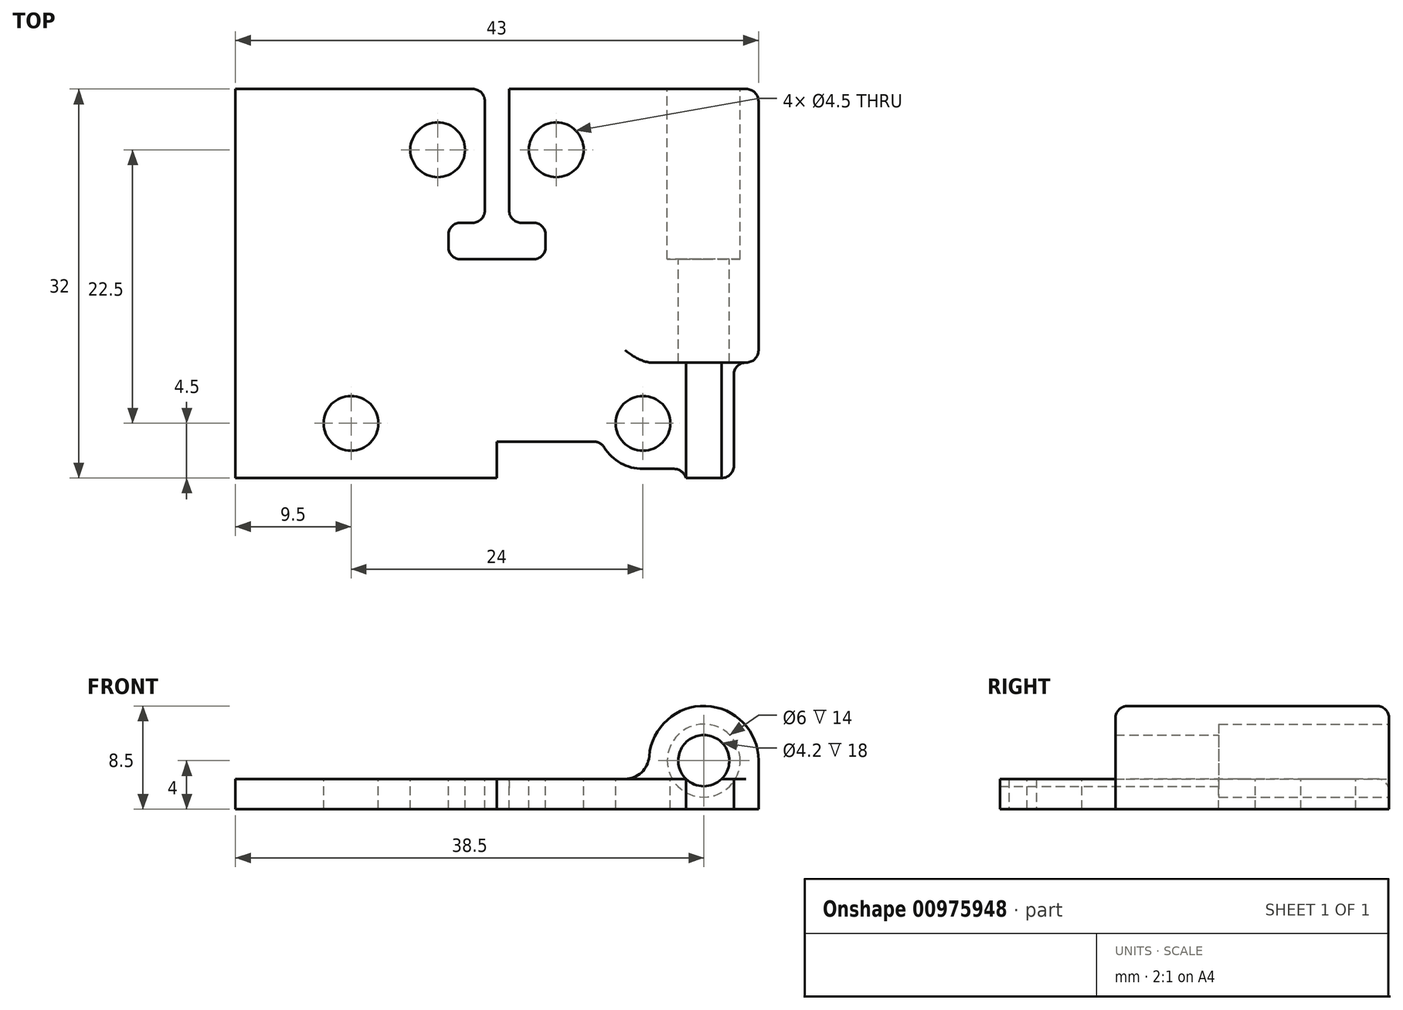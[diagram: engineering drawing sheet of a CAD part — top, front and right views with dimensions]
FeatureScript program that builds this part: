
annotation { "Feature Type Name" : "Feature", "Feature Type Description" : "" }
export const myFeature = defineFeature(function(context is Context, id is Id, definition is map)
    precondition{}
    {
        {
            var Q0;
            Q0=qCreatedBy(makeId("Top.planeOp"),FACE);
            var sketch = newSketch(context, id + "F0", { "sketchPlane" : qUnion([Q0])});
            skLineSegment(sketch, "E0.bottom", {"start": v(21.5, -16) * mm, "end": v(-21.5, -16) * mm});
            skLineSegment(sketch, "E0.top", {"start": v(21.5, 16) * mm, "end": v(-21.5, 16) * mm});
            skLineSegment(sketch, "E0.left", {"start": v(21.5, -16) * mm, "end": v(21.5, 16) * mm});
            skLineSegment(sketch, "E0.right", {"start": v(-21.5, -16) * mm, "end": v(-21.5, 16) * mm});
            skPoint(sketch, "E0.middle", {"position": v(0, 0) * mm});
            skSolve(sketch);
        }
        {
            var Q0;
            Q0 = qSketchRegion(id + "F0", true);
            extrude(context, id + "F1", {"entities" : qUnion([Q0]), "depth" : 2.5 * mm, "offsetDistance" : 25 * mm});
        }
        {
            var Q0;
            Q0=makeQuery(id+"F1.opExtrude","SWEPT_FACE",FACE,{"disambiguationData":[OSD([sQuery(id+"F0.wireOp",EDGE,"E0.top")])]});
            var sketch = newSketch(context, id + "F2", { "sketchPlane" : qUnion([Q0])});
            skLineSegment(sketch, "E1", {"start": v(0, 0) * mm, "end": v(0, 2.5) * mm, "construction": true});
            skLineSegment(sketch, "E2", {"start": v(-21.5, 4) * mm, "end": v(-21.5, 0) * mm});
            skLineSegment(sketch, "E3", {"start": v(-21.5, 0) * mm, "end": v(-12.5, 0) * mm});
            skLineSegment(sketch, "E4", {"start": v(-12.5, 0) * mm, "end": v(-12.5, 4) * mm});
            skArc(sketch, "E5.trimOffspring", {"start": v(-12.5, 4) * mm, "mid": v(-17, 8.5) * mm, "end": v(-21.5, 4) * mm});
            skSolve(sketch);
        }
        {
            var Q0;
            Q0 = qSketchRegion(id + "F2", true);
            extrude(context, id + "F3", {"entities" : qUnion([Q0]), "operationType" : NewBodyOperationType.ADD, "oppositeDirection" : true, "depth" : 22.5 * mm, "offsetDistance" : 25 * mm});
        }
        {
            var Q0;
            Q0=makeQuery(id+"F3.boolean.opBoolean","INTERSECT",EDGE,{"derivedFrom":[makeQuery(id+"F1.opExtrude","CAP_FACE",FACE,{"disambiguationData":[OSD([sQuery(id+"F0.wireOp",EDGE,"E0.bottom"),sQuery(id+"F0.wireOp",EDGE,"E0.top"),sQuery(id+"F0.wireOp",EDGE,"E0.left"),sQuery(id+"F0.wireOp",EDGE,"E0.right")])],"isStart":false}),makeQuery(id+"F3.opExtrude","SWEPT_FACE",FACE,{"disambiguationData":[OSD([sQuery(id+"F2.wireOp",EDGE,"E4")])]})]});
            fillet(context, id + "F4", {"entities" : qUnion([Q0]), "radius" : 2 * mm, "tangentPropagation" : true, "allowEdgeOverflow" : false});
        }
        {
            var Q0;
            Q0=makeQuery(id+"F3.boolean.opBoolean","MERGE",FACE,{"derivedFrom":[makeQuery(id+"F1.opExtrude","SWEPT_FACE",FACE,{"disambiguationData":[OSD([sQuery(id+"F0.wireOp",EDGE,"E0.top")])]}),makeQuery(id+"F3.opExtrude","CAP_FACE",FACE,{"disambiguationData":[OSD([sQuery(id+"F2.wireOp",EDGE,"E2"),sQuery(id+"F2.wireOp",EDGE,"E3"),sQuery(id+"F2.wireOp",EDGE,"E4"),sQuery(id+"F2.wireOp",EDGE,"E5.trimOffspring")])],"isStart":true})]});
            var sketch = newSketch(context, id + "F5", { "sketchPlane" : qUnion([Q0])});
            skArc(sketch, "E6.0", {"start": v(-12.51, 4.35) * mm, "mid": v(-17.17, 8.5) * mm, "end": v(-21.5, 4) * mm, "construction": true});
            skCircle(sketch, "E7", {"center": v(-17, 4) * mm, "radius": 3 * mm});
            skSolve(sketch);
        }
        {
            var Q0;
            Q0 = qSketchRegion(id + "F5", true);
            extrude(context, id + "F6", {"entities" : qUnion([Q0]), "operationType" : NewBodyOperationType.REMOVE, "oppositeDirection" : true, "depth" : 14 * mm, "offsetDistance" : 25 * mm});
        }
        {
            var Q0;
            Q0=makeQuery(id+"F6.boolean.opBoolean","COPY",FACE,{"derivedFrom":makeQuery(id+"F6.opExtrude","CAP_FACE",FACE,{"disambiguationData":[OSD([sQuery(id+"F5.wireOp",EDGE,"E7")])],"isStart":false})});
            var sketch = newSketch(context, id + "F7", { "sketchPlane" : qUnion([Q0])});
            skCircle(sketch, "E8", {"center": v(-17, 4) * mm, "radius": 2.1 * mm});
            skSolve(sketch);
        }
        {
            var Q0;
            Q0 = qSketchRegion(id + "F7", true);
            extrude(context, id + "F8", {"entities" : qUnion([Q0]), "operationType" : NewBodyOperationType.REMOVE, "oppositeDirection" : true, "depth" : 25 * mm, "offsetDistance" : 25 * mm});
        }
        {
            var Q0;
            Q0=makeQuery(id+"F1.opExtrude","CAP_FACE",FACE,{"disambiguationData":[OSD([sQuery(id+"F0.wireOp",EDGE,"E0.bottom"),sQuery(id+"F0.wireOp",EDGE,"E0.top"),sQuery(id+"F0.wireOp",EDGE,"E0.left"),sQuery(id+"F0.wireOp",EDGE,"E0.right")])],"isStart":false});
            var sketch = newSketch(context, id + "F9", { "sketchPlane" : qUnion([Q0])});
            skLineSegment(sketch, "E9", {"start": v(0, 16) * mm, "end": v(0, 0) * mm, "construction": true});
            skPoint(sketch, "E10", {"position": v(12, -11.5) * mm});
            skPoint(sketch, "E11", {"position": v(4.88, 11) * mm});
            skPoint(sketch, "E12.MirrorP", {"position": v(-4.88, 11) * mm});
            skPoint(sketch, "E13.MirrorP", {"position": v(-12, -11.5) * mm});
            skSolve(sketch);
        }
        {
            var Q0;
            Q0=sQuery(id+"F9.wireOp",VERTEX,"E11");
            var Q1;
            Q1=sQuery(id+"F9.wireOp",VERTEX,"E12.MirrorP");
            var Q2;
            Q2=sQuery(id+"F9.wireOp",VERTEX,"E13.MirrorP");
            var Q3;
            Q3=sQuery(id+"F9.wireOp",VERTEX,"E10");
            var Q4;
            Q4=makeQuery(id+"F1.opExtrude","SWEPT_BODY",BODY,{"disambiguationData":[OSD([sQuery(id+"F0.wireOp",EDGE,"E0.bottom"),sQuery(id+"F0.wireOp",EDGE,"E0.top"),sQuery(id+"F0.wireOp",EDGE,"E0.left"),sQuery(id+"F0.wireOp",EDGE,"E0.right")])]});
            hole(context, id + "F10", {"style" : HoleStyle.SIMPLE, "endStyle" : HoleEndStyle.THROUGH, "holeDiameter" : 4.5 * mm, "majorDiameter" : 5 * mm, "isTappedThrough" : true, "tappedDepth" : 12 * mm, "tapClearance" : 3, "locations" : qUnion([Q0, Q1, Q2, Q3]), "scope" : qUnion([Q4])});
        }
        {
            var Q0;
            Q0=makeQuery(id+"F1.opExtrude","CAP_FACE",FACE,{"disambiguationData":[OSD([sQuery(id+"F0.wireOp",EDGE,"E0.bottom"),sQuery(id+"F0.wireOp",EDGE,"E0.top"),sQuery(id+"F0.wireOp",EDGE,"E0.left"),sQuery(id+"F0.wireOp",EDGE,"E0.right")])],"isStart":false});
            var sketch = newSketch(context, id + "F11", { "sketchPlane" : qUnion([Q0])});
            skLineSegment(sketch, "E14", {"start": v(0, 16) * mm, "end": v(0, 0) * mm, "construction": true});
            skLineSegment(sketch, "E15", {"start": v(0, 16) * mm, "end": v(1, 16) * mm});
            skLineSegment(sketch, "E16", {"start": v(1, 16) * mm, "end": v(1, 5) * mm});
            skLineSegment(sketch, "E17", {"start": v(1, 5) * mm, "end": v(4, 5) * mm});
            skLineSegment(sketch, "E18", {"start": v(4, 5) * mm, "end": v(4, 2) * mm});
            skLineSegment(sketch, "E19", {"start": v(4, 2) * mm, "end": v(0, 2) * mm});
            skLineSegment(sketch, "E20.MirrorCS", {"start": v(0, 16) * mm, "end": v(-1, 16) * mm});
            skLineSegment(sketch, "E21.MirrorCS", {"start": v(-1, 16) * mm, "end": v(-1, 5) * mm});
            skLineSegment(sketch, "E22.MirrorCS", {"start": v(-1, 5) * mm, "end": v(-4, 5) * mm});
            skLineSegment(sketch, "E23.MirrorCS", {"start": v(-4, 5) * mm, "end": v(-4, 2) * mm});
            skLineSegment(sketch, "E24.MirrorCS", {"start": v(-4, 2) * mm, "end": v(0, 2) * mm});
            skSolve(sketch);
        }
        {
            var Q0;
            Q0 = qSketchRegion(id + "F11", true);
            extrude(context, id + "F12", {"entities" : qUnion([Q0]), "operationType" : NewBodyOperationType.REMOVE, "endBound" : BoundingType.UP_TO_NEXT, "oppositeDirection" : true, "depth" : 25 * mm, "offsetDistance" : 25 * mm});
        }
        {
            var Q0;
            {var subQ5=sQuery(id+"F0.wireOp",EDGE,"E0.top");var subQ6=makeQuery(id+"F1.opExtrude","SWEPT_FACE",FACE,{"disambiguationData":[OSD([subQ5])]});var subQ8=sQuery(id+"F0.wireOp",EDGE,"E0.bottom");var subQ10=sQuery(id+"F0.wireOp",EDGE,"E0.right");var subQ11=sQuery(id+"F0.wireOp",EDGE,"E0.left");Q0=makeQuery(id+"FoQRUGXMusNffjF_1.1.F8.boolean.opBoolean","SPLIT",FACE,{"disambiguationData":[TD([subQ6])],"derivedFrom":makeQuery(id+"F8.boolean.opBoolean","SPLIT",FACE,{"disambiguationData":[TD([subQ6])],"derivedFrom":makeQuery(id+"F1.opExtrude","CAP_FACE",FACE,{"disambiguationData":[OSD([subQ8,subQ5,subQ11,subQ10])],"isStart":false})})});}
            var sketch = newSketch(context, id + "F13", { "sketchPlane" : qUnion([Q0])});
            skLineSegment(sketch, "E25", {"start": v(0, 0) * mm, "end": v(0, -16) * mm, "construction": true});
            skLineSegment(sketch, "E26.bottom", {"start": v(21.5, -16) * mm, "end": v(19.47, -16) * mm});
            skLineSegment(sketch, "E26.top", {"start": v(21.5, -6.5) * mm, "end": v(19.47, -6.5) * mm});
            skLineSegment(sketch, "E26.left", {"start": v(21.5, -16) * mm, "end": v(21.5, -6.5) * mm});
            skLineSegment(sketch, "E26.right", {"start": v(19.47, -16) * mm, "end": v(19.47, -6.5) * mm});
            skArc(sketch, "E27.0", {"start": v(8.56, -13) * mm, "mid": v(9.95, -14.64) * mm, "end": v(12, -15.25) * mm});
            skLineSegment(sketch, "E28", {"start": v(12, -15.25) * mm, "end": v(15.53, -15.25) * mm});
            skLineSegment(sketch, "E29", {"start": v(0, -13) * mm, "end": v(8.56, -13) * mm});
            skLineSegment(sketch, "E30", {"start": v(0, -13) * mm, "end": v(0, -16) * mm});
            skLineSegment(sketch, "E31", {"start": v(0, -16) * mm, "end": v(15.53, -16) * mm});
            skLineSegment(sketch, "E32", {"start": v(15.53, -16) * mm, "end": v(15.53, -15.25) * mm});
            skSolve(sketch);
        }
        {
            var Q0;
            Q0 = qSketchRegion(id + "F13", true);
            extrude(context, id + "F14", {"entities" : qUnion([Q0]), "operationType" : NewBodyOperationType.REMOVE, "endBound" : BoundingType.UP_TO_NEXT, "oppositeDirection" : true, "depth" : 25 * mm, "offsetDistance" : 25 * mm});
        }
        {
            var Q0;
            Q0=makeQuery(id+"F14.boolean.opBoolean","COPY",EDGE,{"derivedFrom":makeQuery(id+"F14.opExtrude","SWEPT_EDGE",EDGE,{"disambiguationData":[OSD([sQuery(id+"F13.wireOp",EDGE,"E26.top"),sQuery(id+"F13.wireOp",EDGE,"E26.right")])]})});
            var Q1;
            Q1=makeQuery(id+"F14.boolean.opBoolean","COPY",EDGE,{"derivedFrom":makeQuery(id+"F14.opExtrude","SWEPT_EDGE",EDGE,{"disambiguationData":[OSD([sQuery(id+"F13.wireOp",EDGE,"E26.bottom"),sQuery(id+"F13.wireOp",EDGE,"E26.right")])]})});
            var Q2;
            Q2=makeQuery(id+"F14.boolean.opBoolean","COPY",EDGE,{"derivedFrom":makeQuery(id+"F14.opExtrude","SWEPT_EDGE",EDGE,{"disambiguationData":[OSD([sQuery(id+"F13.wireOp",EDGE,"E27.0"),sQuery(id+"F13.wireOp",EDGE,"E29")])]})});
            var Q3;
            Q3=makeQuery(id+"F14.boolean.opBoolean","COPY",EDGE,{"derivedFrom":makeQuery(id+"F14.opExtrude","SWEPT_EDGE",EDGE,{"disambiguationData":[OSD([sQuery(id+"F0.wireOp",EDGE,"E0.bottom"),sQuery(id+"F0.wireOp",EDGE,"E0.top"),sQuery(id+"F0.wireOp",EDGE,"E0.left"),sQuery(id+"F0.wireOp",EDGE,"E0.right"),sQuery(id+"F7.wireOp",EDGE,"E8"),sQuery(id+"F13.wireOp",EDGE,"E28"),sQuery(id+"F13.wireOp",EDGE,"E32")])]})});
            var Q4;
            Q4=makeQuery(id+"FNa3ekNziphppCJ_1.1.F14.boolean.opBoolean","COPY",EDGE,{"derivedFrom":makeQuery(id+"FNa3ekNziphppCJ_1.1.F14.opExtrude","SWEPT_EDGE",EDGE,{"disambiguationData":[OSD([sQuery(id+"F13.wireOp",EDGE,"E27.0"),sQuery(id+"F13.wireOp",EDGE,"E29")])]})});
            var Q5;
            Q5=makeQuery(id+"FNa3ekNziphppCJ_1.1.F14.boolean.opBoolean","COPY",EDGE,{"derivedFrom":makeQuery(id+"FNa3ekNziphppCJ_1.1.F14.opExtrude","SWEPT_EDGE",EDGE,{"disambiguationData":[OSD([sQuery(id+"F13.wireOp",EDGE,"E27.0"),sQuery(id+"F13.wireOp",EDGE,"E28")])]})});
            var Q6;
            Q6=makeQuery(id+"FNa3ekNziphppCJ_1.1.F14.boolean.opBoolean","COPY",EDGE,{"derivedFrom":makeQuery(id+"FNa3ekNziphppCJ_1.1.F14.opExtrude","SWEPT_EDGE",EDGE,{"disambiguationData":[OSD([sQuery(id+"F0.wireOp",EDGE,"E0.bottom"),sQuery(id+"F0.wireOp",EDGE,"E0.top"),sQuery(id+"F0.wireOp",EDGE,"E0.left"),sQuery(id+"F0.wireOp",EDGE,"E0.right"),sQuery(id+"F7.wireOp",EDGE,"E8"),sQuery(id+"F13.wireOp",EDGE,"E28"),sQuery(id+"F13.wireOp",EDGE,"E32")])]})});
            var Q7;
            Q7=makeQuery(id+"FNa3ekNziphppCJ_1.1.F14.boolean.opBoolean","COPY",EDGE,{"derivedFrom":makeQuery(id+"FNa3ekNziphppCJ_1.1.F14.opExtrude","SWEPT_EDGE",EDGE,{"disambiguationData":[OSD([sQuery(id+"F13.wireOp",EDGE,"E26.bottom"),sQuery(id+"F13.wireOp",EDGE,"E26.right")])]})});
            var Q8;
            Q8=makeQuery(id+"FNa3ekNziphppCJ_1.1.F14.boolean.opBoolean","COPY",EDGE,{"derivedFrom":makeQuery(id+"FNa3ekNziphppCJ_1.1.F14.opExtrude","SWEPT_EDGE",EDGE,{"disambiguationData":[OSD([sQuery(id+"F13.wireOp",EDGE,"E26.top"),sQuery(id+"F13.wireOp",EDGE,"E26.right")])]})});
            fillet(context, id + "F15", {"entities" : qUnion([Q0, Q1, Q2, Q3, Q4, Q5, Q6, Q7, Q8]), "radius" : 1 * mm, "tangentPropagation" : true, "allowEdgeOverflow" : false});
        }
        {
            var Q0;
            Q0=makeQuery(id+"F3.opExtrude","CAP_EDGE",EDGE,{"disambiguationData":[OSD([sQuery(id+"F2.wireOp",EDGE,"E5.trimOffspring")])],"isStart":false});
            var Q1;
            {var subQ0=sQuery(id+"F2.wireOp",EDGE,"E2");Q1=makeQuery(id+"F14.boolean.opBoolean","MERGE",EDGE,{"derivedFrom":[makeQuery(id+"F3.opExtrude","CAP_EDGE",EDGE,{"disambiguationData":[OSD([subQ0])],"isStart":false})],"fromTools":[makeQuery(id+"F14.opExtrude","SWEPT_EDGE",EDGE,{"disambiguationData":[OSD([sQuery(id+"F0.wireOp",EDGE,"E0.bottom"),sQuery(id+"F0.wireOp",EDGE,"E0.top"),sQuery(id+"F0.wireOp",EDGE,"E0.left"),sQuery(id+"F0.wireOp",EDGE,"E0.right"),subQ0,sQuery(id+"F2.wireOp",EDGE,"E3"),sQuery(id+"F2.wireOp",EDGE,"E4"),sQuery(id+"F2.wireOp",EDGE,"E5.trimOffspring"),sQuery(id+"F13.wireOp",EDGE,"E26.top"),sQuery(id+"F13.wireOp",EDGE,"E26.left")])]})]});}
            var Q2;
            Q2=makeQuery(id+"F3.boolean.opBoolean","MERGE",EDGE,{"derivedFrom":[makeQuery(id+"F1.opExtrude","SWEPT_EDGE",EDGE,{"disambiguationData":[OSD([sQuery(id+"F0.wireOp",EDGE,"E0.top"),sQuery(id+"F0.wireOp",EDGE,"E0.left")])]}),makeQuery(id+"F3.opExtrude","CAP_EDGE",EDGE,{"disambiguationData":[OSD([sQuery(id+"F2.wireOp",EDGE,"E2")])],"isStart":true})]});
            var Q3;
            Q3=makeQuery(id+"FoQRUGXMusNffjF_1.1.F3.opExtrude","CAP_EDGE",EDGE,{"disambiguationData":[OSD([sQuery(id+"F2.wireOp",EDGE,"E5.trimOffspring")])],"isStart":false});
            var Q4;
            Q4=makeQuery(id+"FoQRUGXMusNffjF_1.1.F3.opExtrude","CAP_EDGE",EDGE,{"disambiguationData":[OSD([sQuery(id+"F2.wireOp",EDGE,"E5.trimOffspring")])],"isStart":true});
            fillet(context, id + "F16", {"entities" : qUnion([Q0, Q1, Q2, Q3, Q4]), "radius" : 1 * mm, "tangentPropagation" : true, "allowEdgeOverflow" : false});
        }
        {
            var Q0;
            Q0=makeQuery(id+"F12.boolean.opBoolean","COPY",EDGE,{"derivedFrom":makeQuery(id+"F12.opExtrude","SWEPT_EDGE",EDGE,{"disambiguationData":[OSD([sQuery(id+"F11.wireOp",EDGE,"E16"),sQuery(id+"F11.wireOp",EDGE,"E17")])]})});
            var Q1;
            Q1=makeQuery(id+"F12.boolean.opBoolean","COPY",EDGE,{"derivedFrom":makeQuery(id+"F12.opExtrude","SWEPT_EDGE",EDGE,{"disambiguationData":[OSD([sQuery(id+"F11.wireOp",EDGE,"E17"),sQuery(id+"F11.wireOp",EDGE,"E18")])]})});
            var Q2;
            Q2=makeQuery(id+"F12.boolean.opBoolean","COPY",EDGE,{"derivedFrom":makeQuery(id+"F12.opExtrude","SWEPT_EDGE",EDGE,{"disambiguationData":[OSD([sQuery(id+"F11.wireOp",EDGE,"E18"),sQuery(id+"F11.wireOp",EDGE,"E19")])]})});
            var Q3;
            Q3=makeQuery(id+"F12.boolean.opBoolean","COPY",EDGE,{"derivedFrom":makeQuery(id+"F12.opExtrude","SWEPT_EDGE",EDGE,{"disambiguationData":[OSD([sQuery(id+"F0.wireOp",EDGE,"E0.top"),sQuery(id+"F11.wireOp",EDGE,"E15"),sQuery(id+"F11.wireOp",EDGE,"E16")])]})});
            var Q4;
            Q4=makeQuery(id+"F12.boolean.opBoolean","COPY",EDGE,{"derivedFrom":makeQuery(id+"F12.opExtrude","SWEPT_EDGE",EDGE,{"disambiguationData":[OSD([sQuery(id+"F0.wireOp",EDGE,"E0.top"),sQuery(id+"F11.wireOp",EDGE,"E20.MirrorCS"),sQuery(id+"F11.wireOp",EDGE,"E21.MirrorCS")])]})});
            var Q5;
            Q5=makeQuery(id+"F12.boolean.opBoolean","COPY",EDGE,{"derivedFrom":makeQuery(id+"F12.opExtrude","SWEPT_EDGE",EDGE,{"disambiguationData":[OSD([sQuery(id+"F11.wireOp",EDGE,"E21.MirrorCS"),sQuery(id+"F11.wireOp",EDGE,"E22.MirrorCS")])]})});
            var Q6;
            Q6=makeQuery(id+"F12.boolean.opBoolean","COPY",EDGE,{"derivedFrom":makeQuery(id+"F12.opExtrude","SWEPT_EDGE",EDGE,{"disambiguationData":[OSD([sQuery(id+"F11.wireOp",EDGE,"E22.MirrorCS"),sQuery(id+"F11.wireOp",EDGE,"E23.MirrorCS")])]})});
            var Q7;
            Q7=makeQuery(id+"F12.boolean.opBoolean","COPY",EDGE,{"derivedFrom":makeQuery(id+"F12.opExtrude","SWEPT_EDGE",EDGE,{"disambiguationData":[OSD([sQuery(id+"F11.wireOp",EDGE,"E23.MirrorCS"),sQuery(id+"F11.wireOp",EDGE,"E24.MirrorCS")])]})});
            fillet(context, id + "F17", {"entities" : qUnion([Q0, Q1, Q2, Q3, Q4, Q5, Q6, Q7]), "radius" : 1 * mm, "allowEdgeOverflow" : false});
        }
    });
